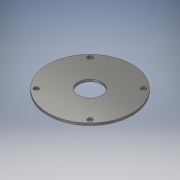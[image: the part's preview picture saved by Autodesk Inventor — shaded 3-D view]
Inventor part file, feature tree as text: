
AUTODESK INVENTOR PART (.ipt)
format: ipt  version: 2018 (Build 220112000, 112)  size: 128,512 bytes
history: native  units: in
note: dims shown in document units (in); Inventor stores cm internally (conversion verified against a paired STEP export)
features: sketch x4, extrude x2, hole x1
ambient origin geometry x8: Origin, YZ Plane, XZ Plane, XY Plane, X Axis, Y Axis, Z Axis, Center Point
bodies: Solid1 (feature_tree)
feature tree (7):
  extrude  "Extrusion1"  Depth=0.1in TaperAngle=0.0deg
  hole  "Hole1"  [1 undecoded]
  sketch  "Sketch3"  dims[d8=0.201in d9=0.5in d10=0.375in d11=0.25in d12=0.5635in d13=1.0in d14=0.8108in d17=3.0in]
  extrude  "Extrusion2"  Depth=0.5in
  sketch  "Sketch1"  dims[d0=1.0in d2=0.1in d3=0.0in]
  sketch  "Sketch2"  dims[d4=2.7in d5=2.7in]
  sketch  "Sketch4"  dims[d18=2.0in d19=3.756in d20=3.6in d21=1.0in d22=0.0in d24=0.2828in]
note: 1 required parameter value undecoded (feature->parameter linkage not recoverable at this tier; creation-order binding heuristic only, values carry confidence <= 0.55)
